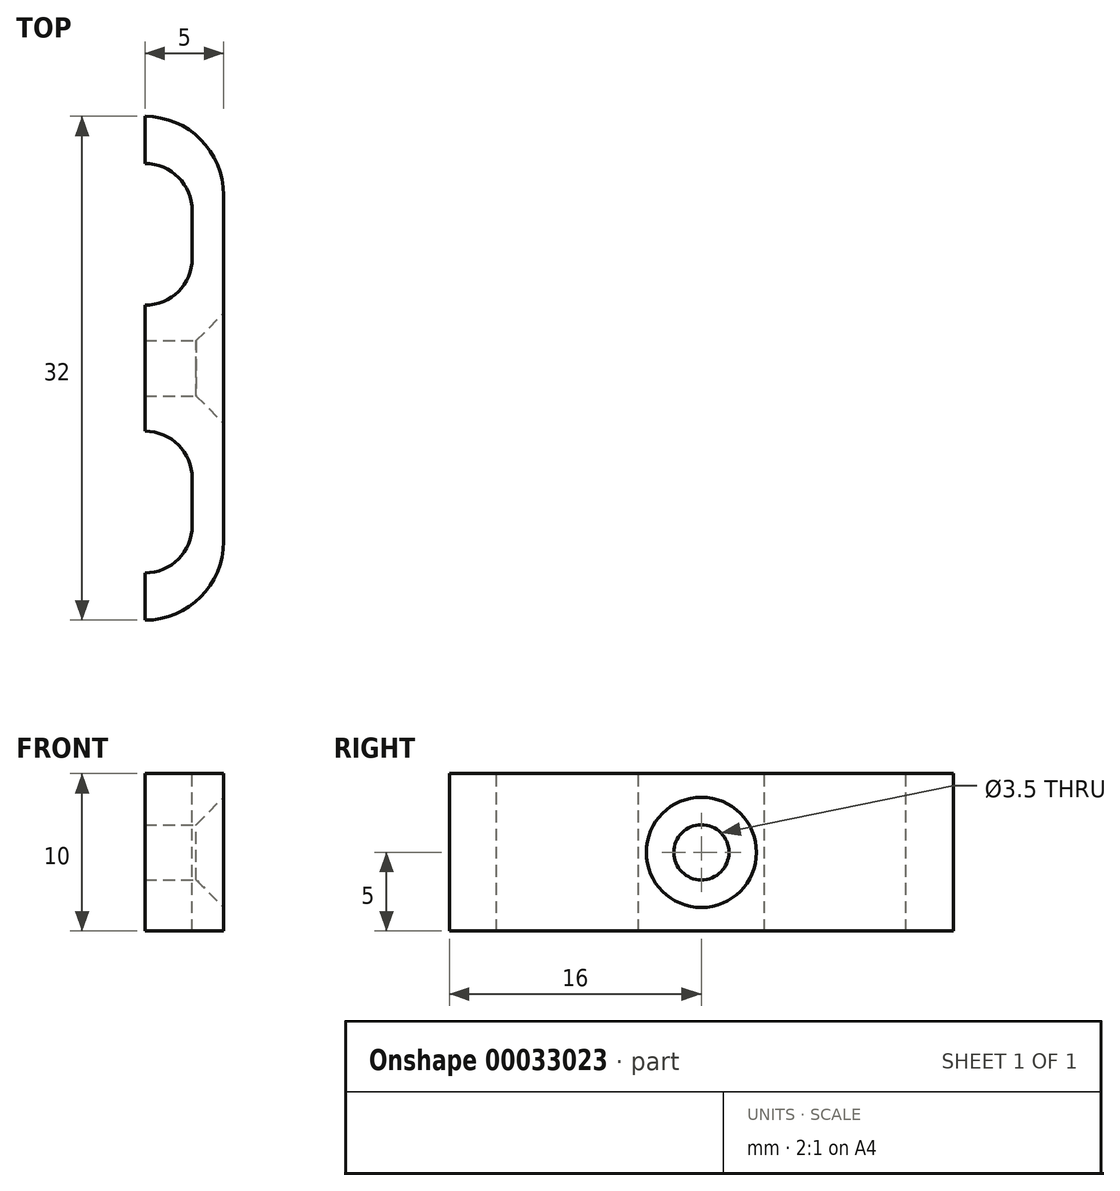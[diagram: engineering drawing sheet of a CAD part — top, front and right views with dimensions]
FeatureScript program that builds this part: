
annotation { "Feature Type Name" : "Feature", "Feature Type Description" : "" }
export const myFeature = defineFeature(function(context is Context, id is Id, definition is map)
    precondition{}
    {
        {
            var Q0;
            Q0=qCreatedBy(makeId("Right.planeOp"),FACE);
            var sketch = newSketch(context, id + "F0", { "sketchPlane" : qUnion([Q0])});
            skLineSegment(sketch, "E0.bottom", {"start": v(-11, 5) * mm, "end": v(0, 5) * mm});
            skLineSegment(sketch, "E0.top", {"start": v(-16, 0) * mm, "end": v(-13, 0) * mm});
            skLineSegment(sketch, "E0.left", {"start": v(-16, 0) * mm, "end": v(-16, 0) * mm});
            skLineSegment(sketch, "E0.right", {"start": v(0, 0) * mm, "end": v(0, 0) * mm});
            skLineSegment(sketch, "E1.top", {"start": v(-10, 3) * mm, "end": v(-7, 3) * mm});
            skLineSegment(sketch, "E1.left", {"start": v(-13, 0) * mm, "end": v(-13, 0) * mm});
            skLineSegment(sketch, "E1.right", {"start": v(-4, 0) * mm, "end": v(-4, 0) * mm});
            skLineSegment(sketch, "E2.trimOffspring", {"start": v(-4, 0) * mm, "end": v(0, 0) * mm});
            skPoint(sketch, "E3.visualSharp", {"position": v(-13, 3) * mm});
            skArc(sketch, "E3.filletArc", {"start": v(-10, 3) * mm, "mid": v(-12.12, 2.12) * mm, "end": v(-13, 0) * mm});
            skPoint(sketch, "E4.visualSharp", {"position": v(-4, 3) * mm});
            skArc(sketch, "E4.filletArc", {"start": v(-4, 0) * mm, "mid": v(-4.88, 2.12) * mm, "end": v(-7, 3) * mm});
            skPoint(sketch, "E5.visualSharp", {"position": v(-16, 5) * mm});
            skArc(sketch, "E5.filletArc", {"start": v(-11, 5) * mm, "mid": v(-14.54, 3.54) * mm, "end": v(-16, 0) * mm});
            skPoint(sketch, "E6.visualSharp", {"position": v(0, 5) * mm});
            skPoint(sketch, "E7.MirrorP", {"position": v(13, 3) * mm});
            skPoint(sketch, "E8.MirrorP", {"position": v(16, 5) * mm});
            skLineSegment(sketch, "E9.MirrorCS", {"start": v(13, 0) * mm, "end": v(13, 0) * mm});
            skLineSegment(sketch, "E10.MirrorCS", {"start": v(11, 5) * mm, "end": v(0, 5) * mm});
            skLineSegment(sketch, "E11.MirrorCS", {"start": v(4, 0) * mm, "end": v(0, 0) * mm});
            skArc(sketch, "E12.MirrorCS", {"start": v(11, 5) * mm, "mid": v(14.54, 3.54) * mm, "end": v(16, 0) * mm});
            skArc(sketch, "E13.MirrorCS", {"start": v(4, 0) * mm, "mid": v(4.88, 2.12) * mm, "end": v(7, 3) * mm});
            skLineSegment(sketch, "E14.MirrorCS", {"start": v(16, 0) * mm, "end": v(16, 0) * mm});
            skLineSegment(sketch, "E15.MirrorCS", {"start": v(4, 0) * mm, "end": v(4, 0) * mm});
            skLineSegment(sketch, "E16.MirrorCS", {"start": v(10, 3) * mm, "end": v(7, 3) * mm});
            skLineSegment(sketch, "E17.MirrorCS", {"start": v(16, 0) * mm, "end": v(13, 0) * mm});
            skPoint(sketch, "E18.MirrorP", {"position": v(4, 3) * mm});
            skArc(sketch, "E19.MirrorCS", {"start": v(10, 3) * mm, "mid": v(12.12, 2.12) * mm, "end": v(13, 0) * mm});
            skSolve(sketch);
        }
        {
            var Q0;
            Q0=makeQuery(id+"F0.imprint","IMPRINT",FACE,{"disambiguationData":[TD([[makeQuery(id+"F0.imprint","IMPRINT",EDGE,{"derivedFrom":sQuery(id+"F0.wireOp",EDGE,"E0.bottom")}),-1.0]])]});
            extrude(context, id + "F1", {"entities" : qUnion([Q0]), "endBound" : BoundingType.SYMMETRIC, "depth" : 10 * mm});
        }
        {
            var Q0;
            Q0=makeQuery(id+"F1.opExtrude","SWEPT_FACE",FACE,{"disambiguationData":[OSD([sQuery(id+"F0.wireOp",EDGE,"E0.bottom")])]});
            var sketch = newSketch(context, id + "F2", { "sketchPlane" : qUnion([Q0])});
            skPoint(sketch, "E20", {"position": v(0, 0) * mm});
            skSolve(sketch);
        }
        {
            var Q0;
            Q0=sQuery(id+"F2.wireOp",VERTEX,"E20");
            var Q1;
            Q1=makeQuery(id+"F1.opExtrude","SWEPT_BODY",BODY,{"disambiguationData":[OSD([sQuery(id+"F0.wireOp",EDGE,"E0.bottom"),sQuery(id+"F0.wireOp",EDGE,"E0.top"),sQuery(id+"F0.wireOp",EDGE,"E0.left"),sQuery(id+"F0.wireOp",EDGE,"E0.right"),sQuery(id+"F0.wireOp",EDGE,"E1.top"),sQuery(id+"F0.wireOp",EDGE,"E2.trimOffspring"),sQuery(id+"F0.wireOp",EDGE,"E3.filletArc"),sQuery(id+"F0.wireOp",EDGE,"E4.filletArc")])]});
            hole(context, id + "F3", {"style" : HoleStyle.C_SINK, "holeDiameter" : 3.5 * mm, "cSinkDiameter" : 7 * mm, "endStyle" : HoleEndStyle.THROUGH, "locations" : qUnion([Q0]), "scope" : qUnion([Q1]), "cSinkAngle" : 90 * degree});
        }
        {
            var Q0;
            Q0=makeQuery(id+"F1.opExtrude","SWEPT_BODY",BODY,{"disambiguationData":[OSD([sQuery(id+"F0.wireOp",EDGE,"E0.bottom"),sQuery(id+"F0.wireOp",EDGE,"E0.top"),sQuery(id+"F0.wireOp",EDGE,"E1.top"),sQuery(id+"F0.wireOp",EDGE,"E2.trimOffspring"),sQuery(id+"F0.wireOp",EDGE,"E3.filletArc"),sQuery(id+"F0.wireOp",EDGE,"E4.filletArc"),sQuery(id+"F0.wireOp",EDGE,"E5.filletArc"),sQuery(id+"F0.wireOp",EDGE,"E6.filletArc")])]});
            var Q1;
            Q1=makeQuery(id+"F1.opExtrude","CAP_EDGE",EDGE,{"disambiguationData":[OSD([sQuery(id+"F0.wireOp",EDGE,"E2.trimOffspring")])],"isStart":false});
            transform(context, id + "F4", {"entities" : qUnion([Q0]), "transformType" : TransformType.ROTATION, "transformAxis" : qUnion([Q1]), "angle" : 90 * degree, "makeCopy" : false});
        }
    });
